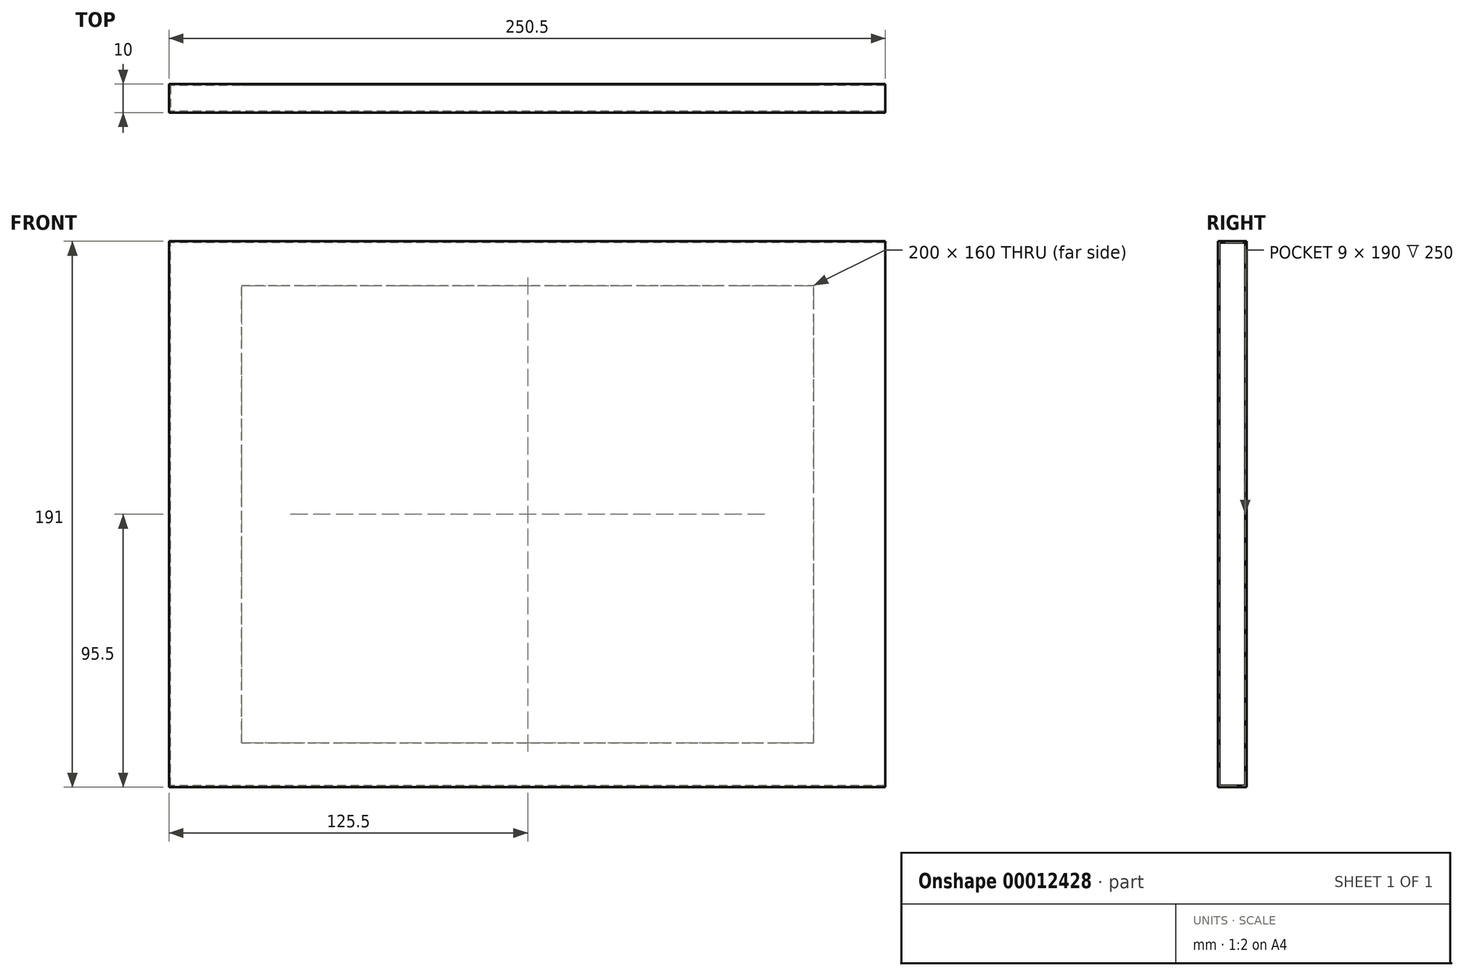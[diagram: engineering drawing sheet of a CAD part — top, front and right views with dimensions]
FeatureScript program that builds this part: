
annotation { "Feature Type Name" : "Feature", "Feature Type Description" : "" }
export const myFeature = defineFeature(function(context is Context, id is Id, definition is map)
    precondition{}
    {
        {
            var Q0;
            Q0=qCreatedBy(makeId("Front.planeOp"),FACE);
            var sketch = newSketch(context, id + "F0", { "sketchPlane" : qUnion([Q0])});
            skLineSegment(sketch, "E0.rect.bottom", {"start": v(125, -95) * mm, "end": v(-125, -95) * mm});
            skLineSegment(sketch, "E0.rect.top", {"start": v(125, 95) * mm, "end": v(-125, 95) * mm});
            skLineSegment(sketch, "E0.rect.left", {"start": v(125, -95) * mm, "end": v(125, 95) * mm});
            skLineSegment(sketch, "E0.rect.right", {"start": v(-125, -95) * mm, "end": v(-125, 95) * mm});
            skPoint(sketch, "E0.rect.middle", {"position": v(0, 0) * mm});
            skSolve(sketch);
        }
        {
            var Q0;
            Q0=makeQuery(id+"F0.imprint","IMPRINT",FACE,{"disambiguationData":[TD([[makeQuery(id+"F0.imprint","IMPRINT",EDGE,{"derivedFrom":sQuery(id+"F0.wireOp",EDGE,"E0.rect.bottom")}),-1.0]])]});
            extrude(context, id + "F1", {"entities" : qUnion([Q0]), "oppositeDirection" : true, "depth" : 9 * mm});
        }
        {
            var Q0;
            Q0=makeQuery(id+"F1.opExtrude","SWEPT_FACE",FACE,{"disambiguationData":[OSD([sQuery(id+"F0.wireOp",EDGE,"E0.rect.left")])]});
            shell(context, id + "F2", {"entities" : qUnion([Q0]), "thickness" : 0.5 * mm, "oppositeDirection" : true});
        }
        {
            var Q0;
            Q0=makeQuery(id+"F1.opExtrude","CAP_FACE",FACE,{"disambiguationData":[OSD([sQuery(id+"F0.wireOp",EDGE,"E0.rect.bottom"),sQuery(id+"F0.wireOp",EDGE,"E0.rect.top"),sQuery(id+"F0.wireOp",EDGE,"E0.rect.left"),sQuery(id+"F0.wireOp",EDGE,"E0.rect.right")])],"isStart":false});
            var sketch = newSketch(context, id + "F3", { "sketchPlane" : qUnion([Q0])});
            skLineSegment(sketch, "E1.rect.bottom", {"start": v(100, -80) * mm, "end": v(-100, -80) * mm});
            skLineSegment(sketch, "E1.rect.top", {"start": v(100, 80) * mm, "end": v(-100, 80) * mm});
            skLineSegment(sketch, "E1.rect.left", {"start": v(100, -80) * mm, "end": v(100, 80) * mm});
            skLineSegment(sketch, "E1.rect.right", {"start": v(-100, -80) * mm, "end": v(-100, 80) * mm});
            skPoint(sketch, "E1.rect.middle", {"position": v(0, 0) * mm});
            skSolve(sketch);
        }
        {
            var Q0;
            Q0=makeQuery(id+"F3.imprint","IMPRINT",FACE,{"disambiguationData":[TD([[makeQuery(id+"F3.imprint","IMPRINT",EDGE,{"derivedFrom":sQuery(id+"F3.wireOp",EDGE,"E1.rect.bottom")}),-1.0]])]});
            extrude(context, id + "F4", {"entities" : qUnion([Q0]), "operationType" : NewBodyOperationType.REMOVE, "oppositeDirection" : true, "depth" : 5 * mm});
        }
    });
